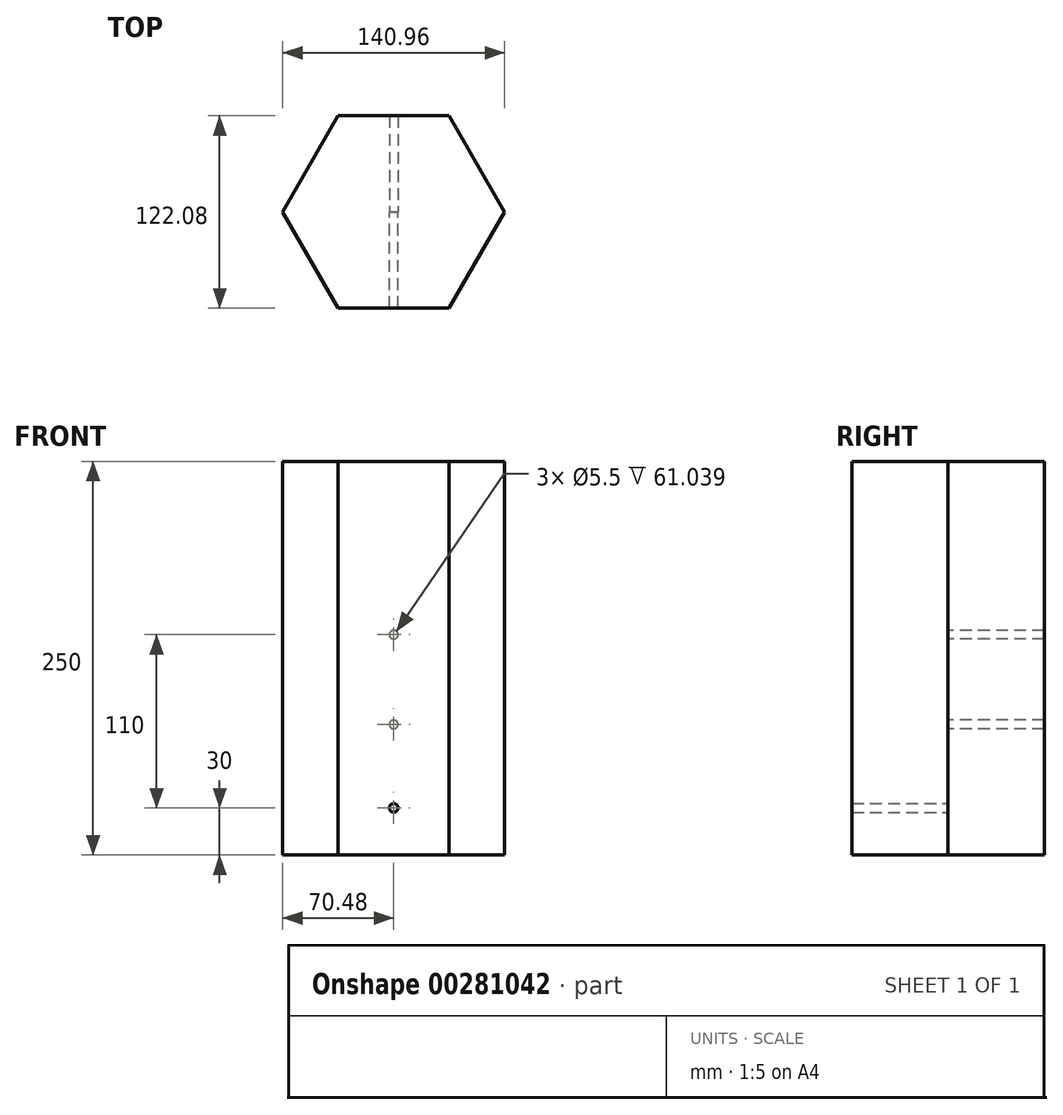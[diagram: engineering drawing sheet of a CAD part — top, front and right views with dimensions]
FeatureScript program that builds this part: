
annotation { "Feature Type Name" : "Feature", "Feature Type Description" : "" }
export const myFeature = defineFeature(function(context is Context, id is Id, definition is map)
    precondition{}
    {
        {
            var Q0;
            Q0=qCreatedBy(makeId("Top.planeOp"),FACE);
            var sketch = newSketch(context, id + "F0", { "sketchPlane" : qUnion([Q0])});
            skCircle(sketch, "E0.cCircle", {"center": v(0, 0) * mm, "radius": 70.48 * mm, "construction": true});
            skLineSegment(sketch, "E0.0", {"start": v(70.48, 0) * mm, "end": v(35.24, -61.04) * mm});
            skLineSegment(sketch, "E0.1", {"start": v(35.24, -61.04) * mm, "end": v(-35.24, -61.04) * mm});
            skLineSegment(sketch, "E0.2", {"start": v(-35.24, -61.04) * mm, "end": v(-70.48, 0) * mm});
            skLineSegment(sketch, "E0.3", {"start": v(-70.48, 0) * mm, "end": v(-35.24, 61.04) * mm});
            skLineSegment(sketch, "E0.4", {"start": v(-35.24, 61.04) * mm, "end": v(35.24, 61.04) * mm});
            skLineSegment(sketch, "E0.5", {"start": v(35.24, 61.04) * mm, "end": v(70.48, 0) * mm});
            skSolve(sketch);
        }
        {
            var Q0;
            Q0 = qSketchRegion(id + "F0", true);
            extrude(context, id + "F1", {"entities" : qUnion([Q0]), "depth" : 250 * mm});
        }
        {
            var Q0;
            Q0=qCreatedBy(makeId("Front.planeOp"),FACE);
            var sketch = newSketch(context, id + "F2", { "sketchPlane" : qUnion([Q0])});
            skPoint(sketch, "E1", {"position": v(0, 140) * mm});
            skPoint(sketch, "E2", {"position": v(0, 83) * mm});
            skPoint(sketch, "E3", {"position": v(0, 30) * mm});
            skSolve(sketch);
        }
        {
            var Q0;
            Q0=sQuery(id+"F2.wireOp",VERTEX,"E1");
            var Q1;
            Q1=sQuery(id+"F2.wireOp",VERTEX,"E2");
            var Q2;
            Q2=makeQuery(id+"F1.opExtrude","SWEPT_BODY",BODY,{"disambiguationData":[OSD([sQuery(id+"F0.wireOp",EDGE,"85fb821b-8ead-4db6-b7a3-2b7fb8ed2e40.0"),sQuery(id+"F0.wireOp",EDGE,"85fb821b-8ead-4db6-b7a3-2b7fb8ed2e40.1"),sQuery(id+"F0.wireOp",EDGE,"85fb821b-8ead-4db6-b7a3-2b7fb8ed2e40.2"),sQuery(id+"F0.wireOp",EDGE,"85fb821b-8ead-4db6-b7a3-2b7fb8ed2e40.3"),sQuery(id+"F0.wireOp",EDGE,"85fb821b-8ead-4db6-b7a3-2b7fb8ed2e40.4"),sQuery(id+"F0.wireOp",EDGE,"85fb821b-8ead-4db6-b7a3-2b7fb8ed2e40.5"),sQuery(id+"F0.wireOp",EDGE,"E0.0"),sQuery(id+"F0.wireOp",EDGE,"E0.1"),sQuery(id+"F0.wireOp",EDGE,"E0.2"),sQuery(id+"F0.wireOp",EDGE,"E0.3"),sQuery(id+"F0.wireOp",EDGE,"E0.4"),sQuery(id+"F0.wireOp",EDGE,"E0.5")])]});
            hole(context, id + "F3", {"style" : HoleStyle.SIMPLE, "endStyle" : HoleEndStyle.THROUGH, "holeDiameter" : 5.5 * mm, "tappedDepth" : 12 * mm, "tapClearance" : 3, "locations" : qUnion([Q0, Q1]), "scope" : qUnion([Q2])});
        }
        {
            var Q0;
            Q0=sQuery(id+"F2.wireOp",VERTEX,"E3");
            var Q1;
            Q1=makeQuery(id+"F1.opExtrude","SWEPT_BODY",BODY,{"disambiguationData":[OSD([sQuery(id+"F0.wireOp",EDGE,"85fb821b-8ead-4db6-b7a3-2b7fb8ed2e40.0"),sQuery(id+"F0.wireOp",EDGE,"85fb821b-8ead-4db6-b7a3-2b7fb8ed2e40.1"),sQuery(id+"F0.wireOp",EDGE,"85fb821b-8ead-4db6-b7a3-2b7fb8ed2e40.2"),sQuery(id+"F0.wireOp",EDGE,"85fb821b-8ead-4db6-b7a3-2b7fb8ed2e40.3"),sQuery(id+"F0.wireOp",EDGE,"85fb821b-8ead-4db6-b7a3-2b7fb8ed2e40.4"),sQuery(id+"F0.wireOp",EDGE,"85fb821b-8ead-4db6-b7a3-2b7fb8ed2e40.5"),sQuery(id+"F0.wireOp",EDGE,"E0.0"),sQuery(id+"F0.wireOp",EDGE,"E0.1"),sQuery(id+"F0.wireOp",EDGE,"E0.2"),sQuery(id+"F0.wireOp",EDGE,"E0.3"),sQuery(id+"F0.wireOp",EDGE,"E0.4"),sQuery(id+"F0.wireOp",EDGE,"E0.5")])]});
            hole(context, id + "F4", {"style" : HoleStyle.SIMPLE, "endStyle" : HoleEndStyle.THROUGH, "oppositeDirection" : true, "holeDiameter" : 5.5 * mm, "tappedDepth" : 12 * mm, "tapClearance" : 3, "locations" : qUnion([Q0]), "scope" : qUnion([Q1])});
        }
    });
